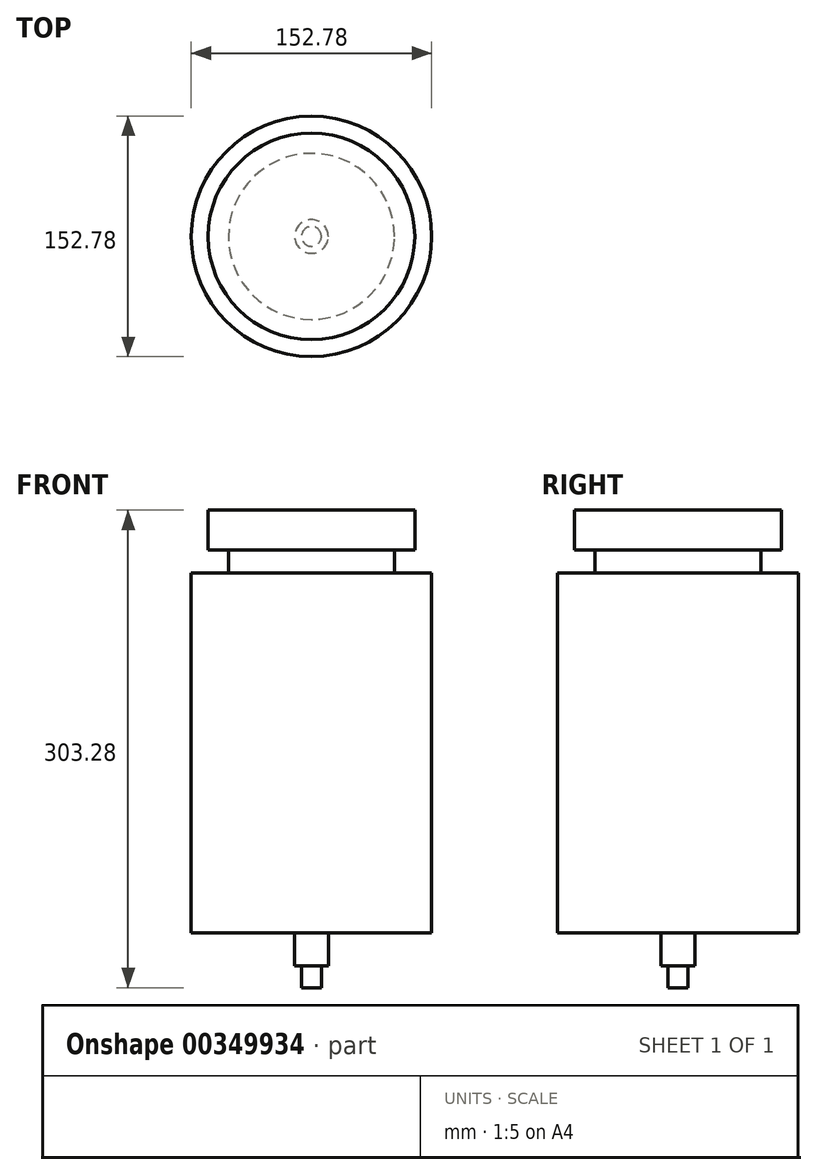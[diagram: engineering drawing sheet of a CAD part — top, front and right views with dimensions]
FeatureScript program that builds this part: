
annotation { "Feature Type Name" : "Feature", "Feature Type Description" : "" }
export const myFeature = defineFeature(function(context is Context, id is Id, definition is map)
    precondition{}
    {
        {
            var Q0;
            Q0=qCreatedBy(makeId("Top.planeOp"),FACE);
            var sketch = newSketch(context, id + "F0", { "sketchPlane" : qUnion([Q0])});
            skCircle(sketch, "E0", {"center": v(0, 0) * mm, "radius": 76.39 * mm});
            skSolve(sketch);
        }
        {
            var Q0;
            Q0 = qSketchRegion(id + "F0", true);
            extrude(context, id + "F1", {"entities" : qUnion([Q0]), "depth" : 228.6 * mm, "offsetDistance" : 25.4 * mm});
        }
        {
            var Q0;
            Q0=makeQuery(id+"F1.opExtrude","CAP_FACE",FACE,{"disambiguationData":[OSD([sQuery(id+"F0.wireOp",EDGE,"E0")])],"isStart":false});
            var sketch = newSketch(context, id + "F2", { "sketchPlane" : qUnion([Q0])});
            skCircle(sketch, "E1", {"center": v(0, 0) * mm, "radius": 52.73 * mm});
            skSolve(sketch);
        }
        {
            var Q0;
            Q0 = qSketchRegion(id + "F2", true);
            extrude(context, id + "F3", {"entities" : qUnion([Q0]), "operationType" : NewBodyOperationType.ADD, "depth" : 14.48 * mm, "offsetDistance" : 25.4 * mm});
        }
        {
            var Q0;
            Q0=makeQuery(id+"F3.opExtrude","CAP_FACE",FACE,{"disambiguationData":[OSD([sQuery(id+"F2.wireOp",EDGE,"E1")])],"isStart":false});
            var sketch = newSketch(context, id + "F4", { "sketchPlane" : qUnion([Q0])});
            skCircle(sketch, "E2", {"center": v(0, 0) * mm, "radius": 65.6 * mm});
            skSolve(sketch);
        }
        {
            var Q0;
            Q0 = qSketchRegion(id + "F4", true);
            extrude(context, id + "F5", {"entities" : qUnion([Q0]), "operationType" : NewBodyOperationType.ADD, "depth" : 25.4 * mm, "offsetDistance" : 25.4 * mm});
        }
        {
            var Q0;
            Q0=makeQuery(id+"F1.opExtrude","CAP_FACE",FACE,{"disambiguationData":[OSD([sQuery(id+"F0.wireOp",EDGE,"E0")])],"isStart":true});
            var sketch = newSketch(context, id + "F6", { "sketchPlane" : qUnion([Q0])});
            skCircle(sketch, "E3", {"center": v(0, 0) * mm, "radius": 10.68 * mm});
            skSolve(sketch);
        }
        {
            var Q0;
            Q0 = qSketchRegion(id + "F6", true);
            extrude(context, id + "F7", {"entities" : qUnion([Q0]), "operationType" : NewBodyOperationType.ADD, "depth" : 21.08 * mm, "offsetDistance" : 25.4 * mm});
        }
        {
            var Q0;
            Q0=makeQuery(id+"F7.opExtrude","CAP_FACE",FACE,{"disambiguationData":[OSD([sQuery(id+"F6.wireOp",EDGE,"E3")])],"isStart":false});
            var sketch = newSketch(context, id + "F8", { "sketchPlane" : qUnion([Q0])});
            skCircle(sketch, "E4", {"center": v(0, 0) * mm, "radius": 6.3 * mm});
            skSolve(sketch);
        }
        {
            var Q0;
            Q0 = qSketchRegion(id + "F8", true);
            extrude(context, id + "F9", {"entities" : qUnion([Q0]), "operationType" : NewBodyOperationType.ADD, "depth" : 13.72 * mm, "offsetDistance" : 25.4 * mm});
        }
    });
